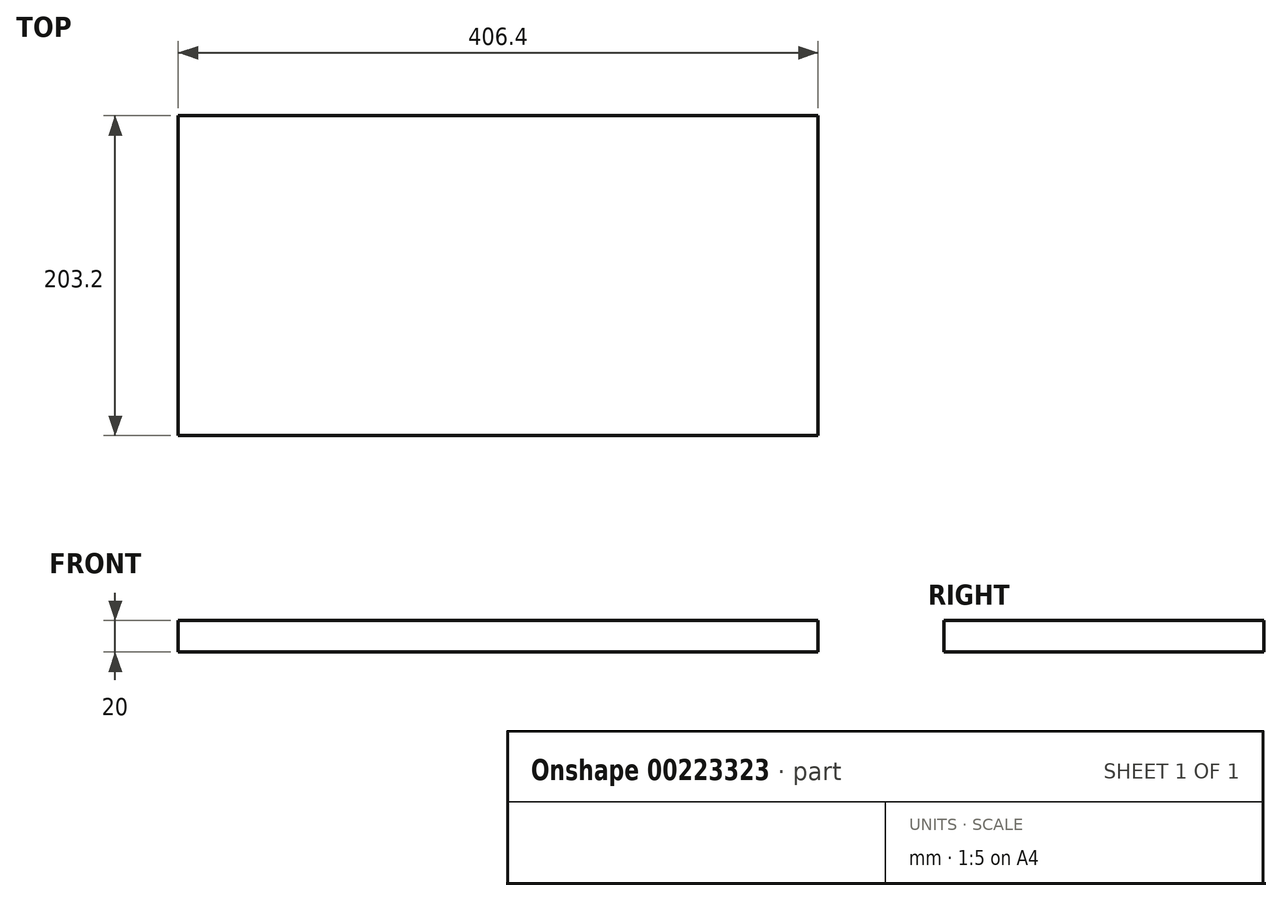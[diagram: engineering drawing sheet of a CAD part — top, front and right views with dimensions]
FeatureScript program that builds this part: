
annotation { "Feature Type Name" : "Feature", "Feature Type Description" : "" }
export const myFeature = defineFeature(function(context is Context, id is Id, definition is map)
    precondition{}
    {
        {
            var Q0;
            Q0=qCreatedBy(makeId("Top.planeOp"),FACE);
            var sketch = newSketch(context, id + "F0", { "sketchPlane" : qUnion([Q0])});
            skLineSegment(sketch, "E0.bottom", {"start": v(203.2, 101.6) * mm, "end": v(-203.2, 101.6) * mm});
            skLineSegment(sketch, "E0.top", {"start": v(203.2, -101.6) * mm, "end": v(-203.2, -101.6) * mm});
            skLineSegment(sketch, "E0.left", {"start": v(203.2, 101.6) * mm, "end": v(203.2, -101.6) * mm});
            skLineSegment(sketch, "E0.right", {"start": v(-203.2, 101.6) * mm, "end": v(-203.2, -101.6) * mm});
            skPoint(sketch, "E0.middle", {"position": v(0, 0) * mm});
            skSolve(sketch);
        }
        {
            var Q0;
            Q0=makeQuery(id+"F0.imprint","IMPRINT",FACE,{"disambiguationData":[TD([[makeQuery(id+"F0.imprint","IMPRINT",EDGE,{"derivedFrom":sQuery(id+"F0.wireOp",EDGE,"E0.bottom")}),1.0]])]});
            extrude(context, id + "F1", {"entities" : qUnion([Q0]), "depth" : 20 * mm, "offsetDistance" : 25 * mm});
        }
    });
